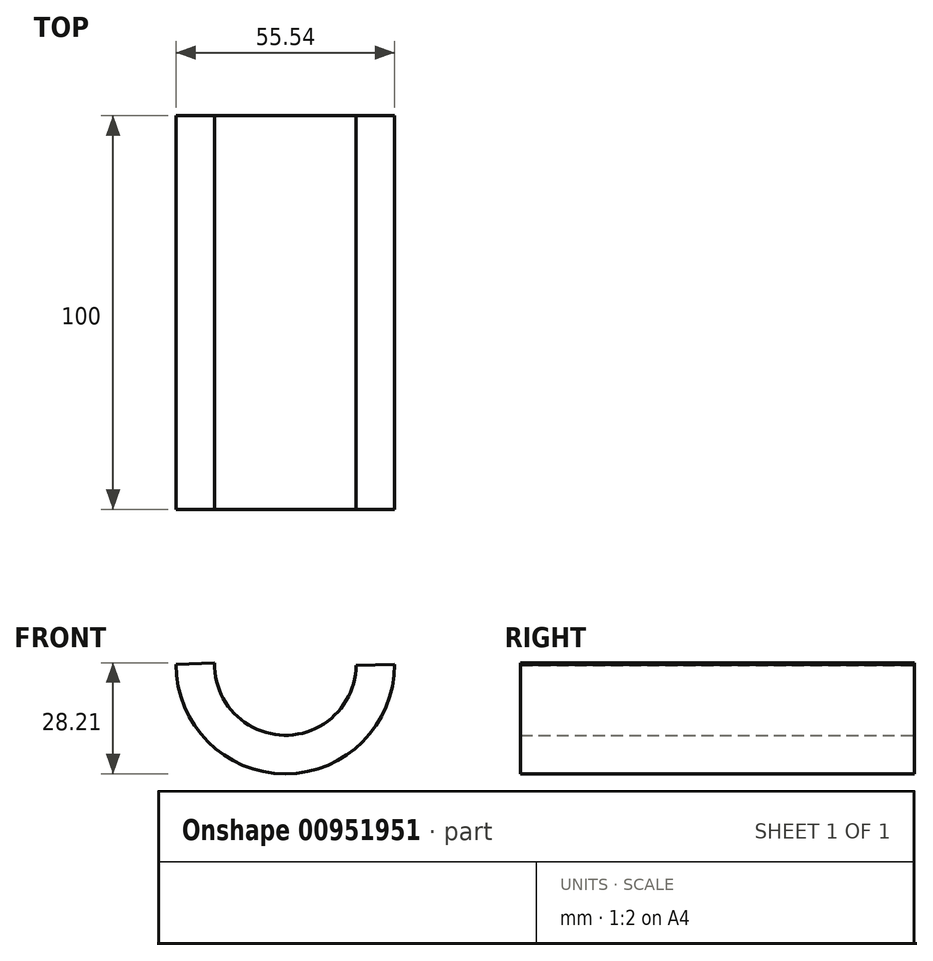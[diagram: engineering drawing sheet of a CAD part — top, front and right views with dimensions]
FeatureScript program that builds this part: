
annotation { "Feature Type Name" : "Feature", "Feature Type Description" : "" }
export const myFeature = defineFeature(function(context is Context, id is Id, definition is map)
    precondition{}
    {
        {
            var Q0;
            Q0=qCreatedBy(makeId("Front.planeOp"),FACE);
            var sketch = newSketch(context, id + "F0", { "sketchPlane" : qUnion([Q0])});
            skArc(sketch, "E0", {"start": v(-17.97, 55.55) * mm, "mid": v(-0.31, 37.14) * mm, "end": v(17.98, 54.92) * mm});
            skArc(sketch, "E1", {"start": v(-27.77, 55.11) * mm, "mid": v(0, 27.34) * mm, "end": v(27.77, 55.11) * mm});
            skLineSegment(sketch, "E2", {"start": v(-27.77, 55.11) * mm, "end": v(-17.97, 55.55) * mm});
            skLineSegment(sketch, "E3", {"start": v(17.98, 54.92) * mm, "end": v(27.77, 55.11) * mm});
            skSolve(sketch);
        }
        {
            var Q0;
            Q0=makeQuery(id+"F0.imprint","IMPRINT",FACE,{"disambiguationData":[TD([[makeQuery(id+"F0.imprint","IMPRINT",EDGE,{"derivedFrom":sQuery(id+"F0.wireOp",EDGE,"E0")}),-1.0]])]});
            extrude(context, id + "F1", {"entities" : qUnion([Q0]), "endBound" : BoundingType.SYMMETRIC, "depth" : 100 * mm, "offsetDistance" : 25 * mm});
        }
    });
